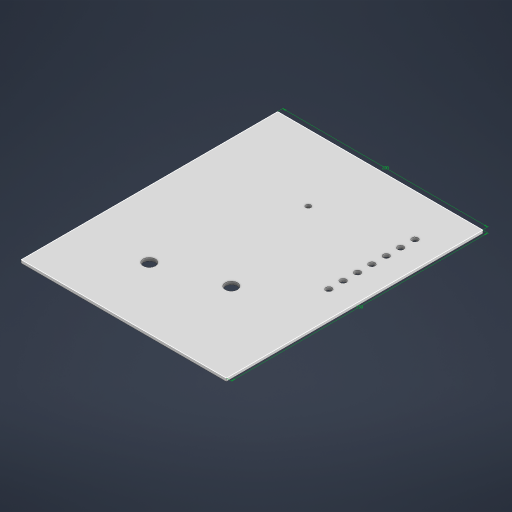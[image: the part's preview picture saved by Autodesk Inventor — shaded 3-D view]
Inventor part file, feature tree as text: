
AUTODESK INVENTOR PART (.ipt)
format: ipt  version: 2023 (Build 270158000, 158)  size: 230,400 bytes
history: native  units: mm
features: extrude x5, sketch x3, other x2, shell x1, plane x1
ambient origin geometry x8: Origin, YZ Plane, XZ Plane, XY Plane, X Axis, Y Axis, Z Axis, Center Point
bodies: Body1 (feature_tree)
feature tree (12):
  other  "block"
  extrude  "ext_block"  Depth=250.0mm
  shell  "Shell2"  Thickness=12.0mm
  extrude  "holes"  Depth=25.0mm
  extrude  "pwr_button_hole"  Depth=3.0mm
  plane  "Work Plane1"
  extrude  "back_cover_cut"  Depth=3.0mm
  extrude  "Extrusion8"  Depth=3.0mm
  other  "lines_base"
  sketch  "Sketch4"  dims[d0=200.0mm d1=250.0mm d2=12.0mm]
  sketch  "Sketch5"  dims[d3=12.0mm d4=25.0mm]
  sketch  "Sketch10"  dims[d5=17.0mm d6=17.0mm d7=25.0mm d8=75.0mm d9=80.0mm d10=65.0mm d11=60.0mm d12=6.0mm d13=84.0mm d14=90.0deg d15=25.0mm d16=125.0mm d17=70.0mm d19=14.0mm d20=10.0mm d22=10.0mm d24=5.0mm d25=10.0mm d26=65.0mm d27=95.0mm d31=200.0mm d32=250.0mm d35=24.0mm d36=0.0mm d37=3.0mm d38=24.0mm d39=0.0mm d40=19.0mm d41=13.0mm d42=4.0mm d43=12.0mm d44=24.0mm d45=0.0mm d49=0.0mm d50=0.0mm d62=0.0mm d63=0.0mm d33=0.5mm d34=0.872665mm d64=0.5mm d65=0.872665mm]
